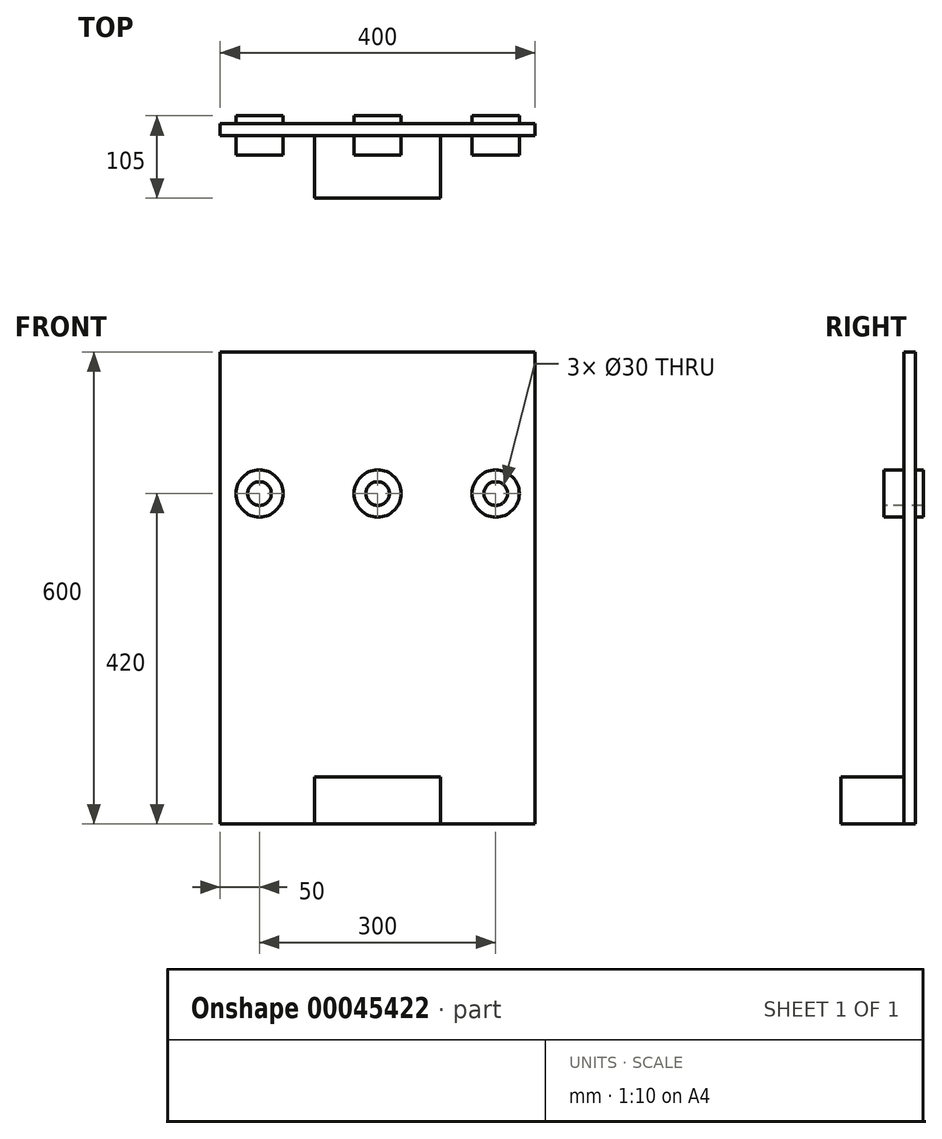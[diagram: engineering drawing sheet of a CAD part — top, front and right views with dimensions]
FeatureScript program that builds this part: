
annotation { "Feature Type Name" : "Feature", "Feature Type Description" : "" }
export const myFeature = defineFeature(function(context is Context, id is Id, definition is map)
    precondition{}
    {
        {
            var Q0;
            Q0=qCreatedBy(makeId("Front.planeOp"),FACE);
            var sketch = newSketch(context, id + "F0", { "sketchPlane" : qUnion([Q0])});
            skLineSegment(sketch, "E0.rect.bottom", {"start": v(-200, 300) * mm, "end": v(200, 300) * mm});
            skLineSegment(sketch, "E0.rect.top", {"start": v(-200, -300) * mm, "end": v(200, -300) * mm});
            skLineSegment(sketch, "E0.rect.left", {"start": v(-200, 300) * mm, "end": v(-200, -300) * mm});
            skLineSegment(sketch, "E0.rect.right", {"start": v(200, 300) * mm, "end": v(200, -300) * mm});
            skPoint(sketch, "E0.rect.middle", {"position": v(0, 0) * mm});
            skSolve(sketch);
        }
        {
            var Q0;
            Q0 = qSketchRegion(id + "F0", true);
            extrude(context, id + "F1", {"entities" : qUnion([Q0]), "oppositeDirection" : true, "depth" : 15 * mm});
        }
        {
            var Q0;
            Q0=makeQuery(id+"F1.opExtrude","CAP_FACE",FACE,{"disambiguationData":[OSD([sQuery(id+"F0.wireOp",EDGE,"E0.rect.bottom"),sQuery(id+"F0.wireOp",EDGE,"E0.rect.top"),sQuery(id+"F0.wireOp",EDGE,"E0.rect.left"),sQuery(id+"F0.wireOp",EDGE,"E0.rect.right")])],"isStart":true});
            var sketch = newSketch(context, id + "F2", { "sketchPlane" : qUnion([Q0])});
            skCircle(sketch, "E1", {"center": v(-150, 120) * mm, "radius": 30 * mm});
            skCircle(sketch, "E2", {"center": v(0, 120) * mm, "radius": 30 * mm});
            skCircle(sketch, "E3", {"center": v(150, 120) * mm, "radius": 30 * mm});
            skCircle(sketch, "E4", {"center": v(-150, 120) * mm, "radius": 15 * mm});
            skCircle(sketch, "E5", {"center": v(0, 120) * mm, "radius": 15 * mm});
            skCircle(sketch, "E6", {"center": v(150, 120) * mm, "radius": 15 * mm});
            skSolve(sketch);
        }
        {
            var Q0;
            Q0 = qSketchRegion(id + "F2", true);
            extrude(context, id + "F3", {"entities" : qUnion([Q0]), "operationType" : NewBodyOperationType.ADD, "endBound" : BoundingType.SYMMETRIC, "oppositeDirection" : true, "depth" : 50 * mm});
        }
        {
            var Q0;
            Q0=makeQuery(id+"F3.boolean.opBoolean","SPLIT",FACE,{"disambiguationData":[TD([makeQuery(id+"F3.opExtrude","SWEPT_FACE",FACE,{"disambiguationData":[OSD([sQuery(id+"F2.wireOp",EDGE,"E6")])]})])],"derivedFrom":makeQuery(id+"F1.opExtrude","CAP_FACE",FACE,{"disambiguationData":[OSD([sQuery(id+"F0.wireOp",EDGE,"E0.rect.bottom"),sQuery(id+"F0.wireOp",EDGE,"E0.rect.top"),sQuery(id+"F0.wireOp",EDGE,"E0.rect.left"),sQuery(id+"F0.wireOp",EDGE,"E0.rect.right")])],"isStart":true})});
            var Q1;
            Q1=makeQuery(id+"F3.boolean.opBoolean","SPLIT",FACE,{"disambiguationData":[TD([makeQuery(id+"F3.opExtrude","SWEPT_FACE",FACE,{"disambiguationData":[OSD([sQuery(id+"F2.wireOp",EDGE,"E5")])]})])],"derivedFrom":makeQuery(id+"F1.opExtrude","CAP_FACE",FACE,{"disambiguationData":[OSD([sQuery(id+"F0.wireOp",EDGE,"E0.rect.bottom"),sQuery(id+"F0.wireOp",EDGE,"E0.rect.top"),sQuery(id+"F0.wireOp",EDGE,"E0.rect.left"),sQuery(id+"F0.wireOp",EDGE,"E0.rect.right")])],"isStart":true})});
            var Q2;
            Q2=makeQuery(id+"F3.boolean.opBoolean","SPLIT",FACE,{"disambiguationData":[TD([makeQuery(id+"F3.opExtrude","SWEPT_FACE",FACE,{"disambiguationData":[OSD([sQuery(id+"F2.wireOp",EDGE,"E4")])]})])],"derivedFrom":makeQuery(id+"F1.opExtrude","CAP_FACE",FACE,{"disambiguationData":[OSD([sQuery(id+"F0.wireOp",EDGE,"E0.rect.bottom"),sQuery(id+"F0.wireOp",EDGE,"E0.rect.top"),sQuery(id+"F0.wireOp",EDGE,"E0.rect.left"),sQuery(id+"F0.wireOp",EDGE,"E0.rect.right")])],"isStart":true})});
            extrude(context, id + "F4", {"entities" : qUnion([Q0, Q1, Q2]), "operationType" : NewBodyOperationType.REMOVE, "endBound" : BoundingType.THROUGH_ALL, "oppositeDirection" : true, "depth" : 25 * mm});
        }
        {
            var Q0;
            {var subQ0=sQuery(id+"F0.wireOp",EDGE,"E0.rect.bottom");var subQ1=sQuery(id+"F0.wireOp",EDGE,"E0.rect.top");var subQ2=sQuery(id+"F0.wireOp",EDGE,"E0.rect.left");var subQ3=sQuery(id+"F0.wireOp",EDGE,"E0.rect.right");Q0=makeQuery(id+"F3.boolean.opBoolean","SPLIT",FACE,{"disambiguationData":[TD([makeQuery(id+"F1.opExtrude","SWEPT_FACE",FACE,{"disambiguationData":[OSD([subQ0])]})])],"derivedFrom":makeQuery(id+"F1.opExtrude","CAP_FACE",FACE,{"disambiguationData":[OSD([subQ0,subQ1,subQ2,subQ3])],"isStart":true})});}
            var sketch = newSketch(context, id + "F5", { "sketchPlane" : qUnion([Q0])});
            skLineSegment(sketch, "E7.bottom", {"start": v(-80, -300) * mm, "end": v(80, -300) * mm});
            skLineSegment(sketch, "E7.top", {"start": v(-80, -240) * mm, "end": v(80, -240) * mm});
            skLineSegment(sketch, "E7.left", {"start": v(-80, -300) * mm, "end": v(-80, -240) * mm});
            skLineSegment(sketch, "E7.right", {"start": v(80, -300) * mm, "end": v(80, -240) * mm});
            skSolve(sketch);
        }
        {
            var Q0;
            Q0 = qSketchRegion(id + "F5", true);
            extrude(context, id + "F6", {"entities" : qUnion([Q0]), "operationType" : NewBodyOperationType.ADD, "depth" : 80 * mm});
        }
    });
